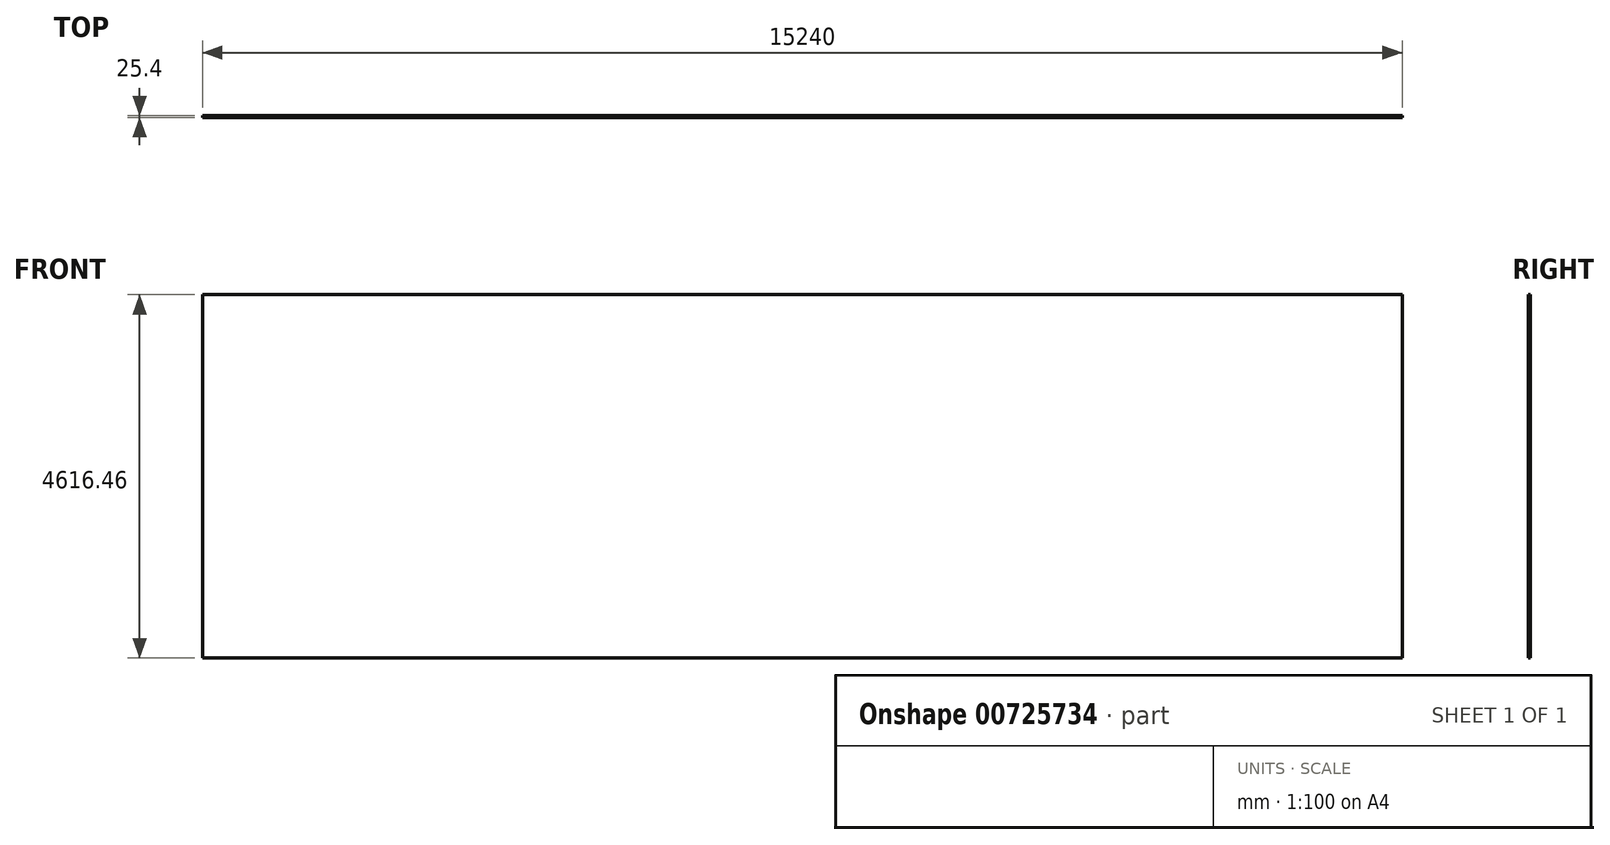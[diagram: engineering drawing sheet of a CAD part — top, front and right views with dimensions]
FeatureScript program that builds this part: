
annotation { "Feature Type Name" : "Feature", "Feature Type Description" : "" }
export const myFeature = defineFeature(function(context is Context, id is Id, definition is map)
    precondition{}
    {
        {
            var Q0;
            Q0=qCreatedBy(makeId("Front.planeOp"),FACE);
            var sketch = newSketch(context, id + "F0", { "sketchPlane" : qUnion([Q0])});
            skLineSegment(sketch, "E0.bottom", {"start": v(7620, -2308.22) * mm, "end": v(-7620, -2308.23) * mm});
            skLineSegment(sketch, "E0.top", {"start": v(7620, 2308.23) * mm, "end": v(-7620, 2308.22) * mm});
            skLineSegment(sketch, "E0.left", {"start": v(7620, -2308.22) * mm, "end": v(7620, 2308.23) * mm});
            skLineSegment(sketch, "E0.right", {"start": v(-7620, -2308.23) * mm, "end": v(-7620, 2308.23) * mm});
            skPoint(sketch, "E0.middle", {"position": v(0, 0) * mm});
            skSolve(sketch);
        }
        {
            var Q0;
            Q0=makeQuery(id+"F0.imprint","IMPRINT",FACE,{"disambiguationData":[TD([[makeQuery(id+"F0.imprint","IMPRINT",EDGE,{"derivedFrom":sQuery(id+"F0.wireOp",EDGE,"E0.bottom")}),-1.0]])]});
            extrude(context, id + "F1", {"entities" : qUnion([Q0]), "depth" : 25.4 * mm, "offsetDistance" : 25.4 * mm});
        }
    });
